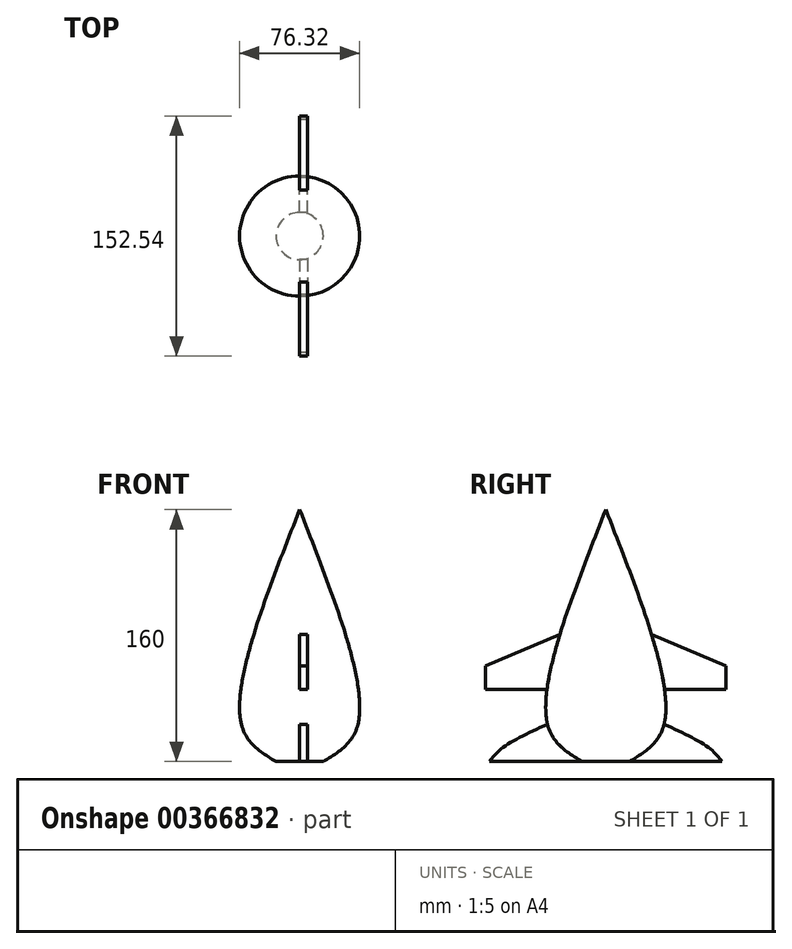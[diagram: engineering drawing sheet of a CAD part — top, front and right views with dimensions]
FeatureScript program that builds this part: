
annotation { "Feature Type Name" : "Feature", "Feature Type Description" : "" }
export const myFeature = defineFeature(function(context is Context, id is Id, definition is map)
    precondition{}
    {
        {
            var Q0;
            Q0=qCreatedBy(makeId("Right.planeOp"),FACE);
            var sketch = newSketch(context, id + "F0", { "sketchPlane" : qUnion([Q0])});
            skLineSegment(sketch, "E0", {"start": v(0, 0) * mm, "end": v(0, 160) * mm});
            skLineSegment(sketch, "E1", {"start": v(0, 0) * mm, "end": v(15, 0) * mm});
            skFitSpline(sketch, "E2", {"points": [v(15, 0) * mm, v(37.03, 23.72) * mm, v(0, 160) * mm], "startDerivative": vector(87.9, 52.5) * mm, "endDerivative": vector(-96.27, 244.9) * mm});
            skLineSegment(sketch, "E3", {"start": v(76.27, 45.86) * mm, "end": v(76.27, 75.86) * mm});
            skFitSpline(sketch, "E4", {"points": [v(76.27, 45.86) * mm, v(92.25, 46.26) * mm, v(76.27, 75.86) * mm], "startDerivative": vector(23.23, 13.8) * mm, "endDerivative": vector(-20, 43.95) * mm});
            skLineSegment(sketch, "E5", {"start": v(76.27, 60.86) * mm, "end": v(29.1, 80.64) * mm});
            skLineSegment(sketch, "E6", {"start": v(76.27, 45.86) * mm, "end": v(37.31, 45.86) * mm});
            skLineSegment(sketch, "E7", {"start": v(15, 0) * mm, "end": v(73.84, 0) * mm});
            skFitSpline(sketch, "E8", {"points": [v(73.84, 0) * mm, v(65.5, 8.72) * mm, v(37.03, 23.72) * mm], "startDerivative": vector(-17.4, 22.73) * mm, "endDerivative": vector(-53.34, 24.56) * mm});
            skSolve(sketch);
        }
        {
            var Q0;
            Q0=makeQuery(id+"F0.imprint","IMPRINT",FACE,{"disambiguationData":[TD([[makeQuery(id+"F0.imprint","IMPRINT",EDGE,{"derivedFrom":sQuery(id+"F0.wireOp",EDGE,"E0")}),-1.0]])]});
            var Q1;
            Q1=sQuery(id+"F0.wireOp",EDGE,"E0");
            revolve(context, id + "F1", {"entities" : qUnion([Q0]), "axis" : qUnion([Q1]), "revolveType" : RevolveType.FULL});
        }
        {
            var Q0;
            Q0=sQuery(id+"F0.wireOp",EDGE,"E4");
            var Q1;
            Q1=sQuery(id+"F0.wireOp",EDGE,"E3");
            revolve(context, id + "F2", {"bodyType" : ToolBodyType.SURFACE, "surfaceEntities" : qUnion([Q0]), "axis" : qUnion([Q1]), "revolveType" : RevolveType.FULL});
        }
        {
            var Q0;
            Q0=makeQuery(id+"F2.opRevolve","SWEPT_BODY",BODY,{"disambiguationData":[OSD([sQuery(id+"F0.wireOp",EDGE,"E4")])]});
            var Q1;
            Q1=qCreatedBy(makeId("Front.planeOp"),FACE);
            mirror(context, id + "F3", {"entities" : qUnion([Q0]), "mirrorPlane" : qUnion([Q1])});
        }
        {
            var Q0;
            {var subQ0=sQuery(id+"F0.wireOp",EDGE,"E5");Q0=makeQuery(id+"F0.imprint","IMPRINT",FACE,{"disambiguationData":[TD([[makeQuery(id+"F0.imprint","IMPRINT",EDGE,{"derivedFrom":subQ0}),1.0]])]});}
            extrude(context, id + "F4", {"entities" : qUnion([Q0]), "depth" : 5 * mm});
        }
        {
            var Q0;
            Q0=makeQuery(id+"F4.opExtrude","SWEPT_BODY",BODY,{"disambiguationData":[OSD([sQuery(id+"F0.wireOp",EDGE,"E2"),sQuery(id+"F0.wireOp",EDGE,"E3"),sQuery(id+"F0.wireOp",EDGE,"E5"),sQuery(id+"F0.wireOp",EDGE,"E6")])]});
            var Q1;
            Q1=qCreatedBy(makeId("Front.planeOp"),FACE);
            mirror(context, id + "F5", {"entities" : qUnion([Q0]), "mirrorPlane" : qUnion([Q1])});
        }
        {
            var Q0;
            {var subQ0=sQuery(id+"F0.wireOp",EDGE,"E7");Q0=makeQuery(id+"F0.imprint","IMPRINT",FACE,{"disambiguationData":[TD([[makeQuery(id+"F0.imprint","IMPRINT",EDGE,{"derivedFrom":subQ0}),1.0]])]});}
            extrude(context, id + "F6", {"entities" : qUnion([Q0]), "depth" : 5 * mm});
        }
        {
            var Q0;
            Q0=makeQuery(id+"F6.opExtrude","SWEPT_BODY",BODY,{"disambiguationData":[OSD([sQuery(id+"F0.wireOp",EDGE,"E2"),sQuery(id+"F0.wireOp",EDGE,"E7"),sQuery(id+"F0.wireOp",EDGE,"E8")])]});
            var Q1;
            Q1=qCreatedBy(makeId("Front.planeOp"),FACE);
            mirror(context, id + "F7", {"entities" : qUnion([Q0]), "mirrorPlane" : qUnion([Q1])});
        }
        {
            var Q0;
            Q0=qCreatedBy(makeId("Front.planeOp"),FACE);
            var sketch = newSketch(context, id + "F8", { "sketchPlane" : qUnion([Q0])});
            skLineSegment(sketch, "E9", {"start": v(16.12, 0) * mm, "end": v(75.01, 0) * mm});
            skFitSpline(sketch, "E10", {"points": [v(75.01, 0) * mm, v(63.1, 7.36) * mm, v(31.2, 12.97) * mm], "startDerivative": vector(-25.5, 20.39) * mm, "endDerivative": vector(-59.76, 6.5) * mm});
            skSolve(sketch);
        }
        {
            var Q0;
            Q0=sQuery(id+"F8.wireOp",EDGE,"E9");
            extrude(context, id + "F9", {"bodyType" : ToolBodyType.SURFACE, "surfaceEntities" : qUnion([Q0]), "depth" : 5 * mm});
        }
    });
